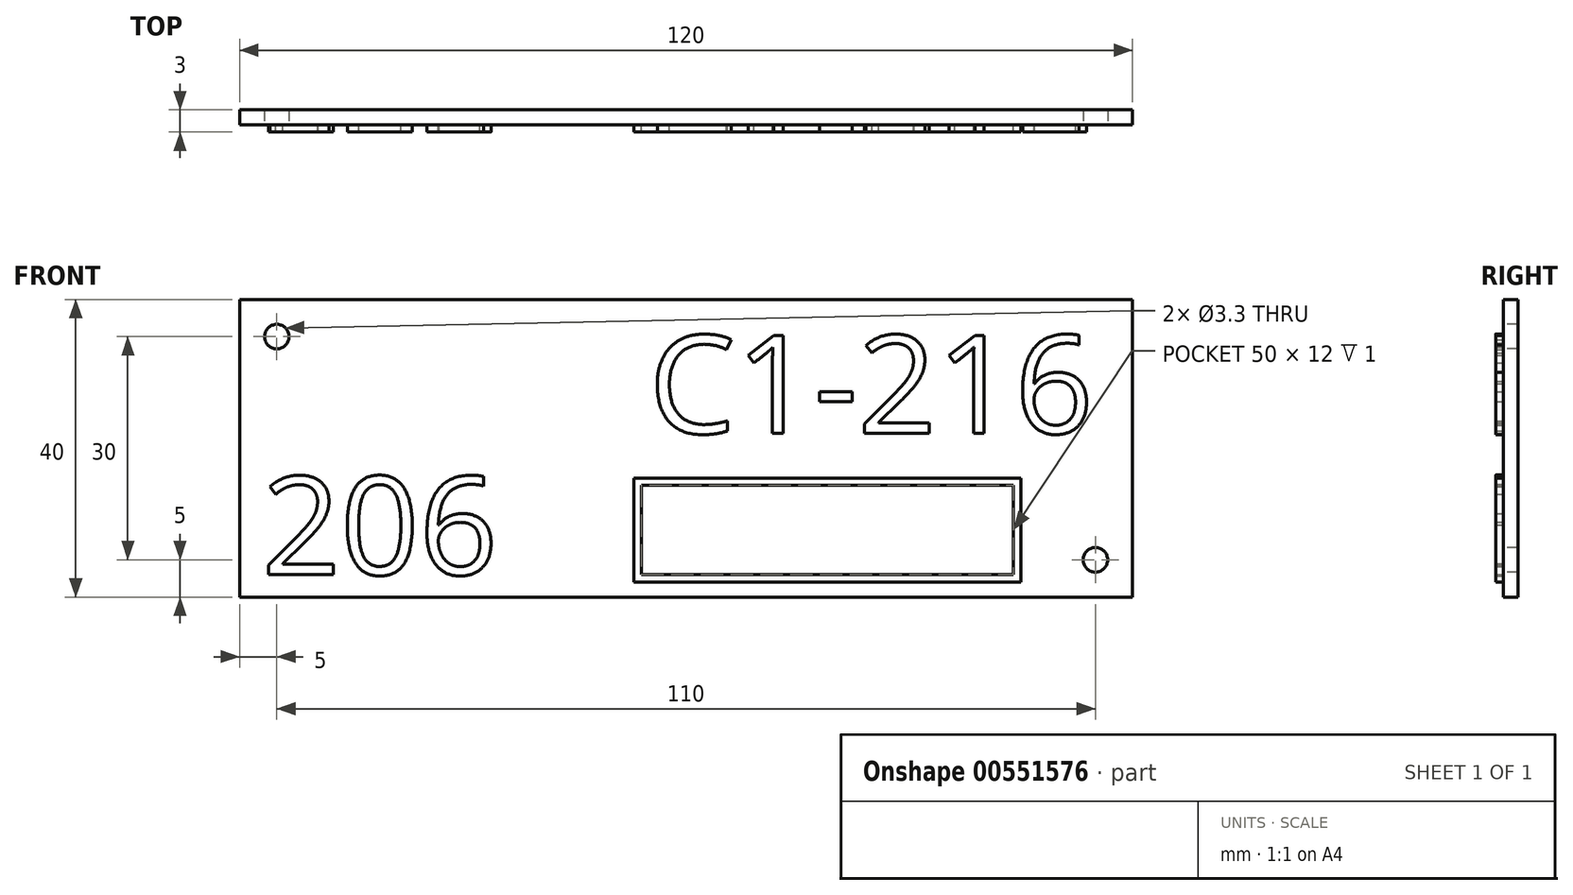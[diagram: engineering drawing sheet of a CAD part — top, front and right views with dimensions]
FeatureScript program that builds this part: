
annotation { "Feature Type Name" : "Feature", "Feature Type Description" : "" }
export const myFeature = defineFeature(function(context is Context, id is Id, definition is map)
    precondition{}
    {
        {
            var Q0;
            Q0=qCreatedBy(makeId("Front.planeOp"),FACE);
            var sketch = newSketch(context, id + "F0", { "sketchPlane" : qUnion([Q0])});
            skLineSegment(sketch, "E0.bottom", {"start": v(60, -20) * mm, "end": v(-60, -20) * mm});
            skLineSegment(sketch, "E0.top", {"start": v(60, 20) * mm, "end": v(-60, 20) * mm});
            skLineSegment(sketch, "E0.left", {"start": v(60, -20) * mm, "end": v(60, 20) * mm});
            skLineSegment(sketch, "E0.right", {"start": v(-60, -20) * mm, "end": v(-60, 20) * mm});
            skPoint(sketch, "E0.middle", {"position": v(0, 0) * mm});
            skSolve(sketch);
        }
        {
            var Q0;
            Q0=makeQuery(id+"F0.imprint","IMPRINT",FACE,{"disambiguationData":[TD([[makeQuery(id+"F0.imprint","IMPRINT",EDGE,{"derivedFrom":sQuery(id+"F0.wireOp",EDGE,"E0.bottom")}),-1.0]])]});
            extrude(context, id + "F1", {"entities" : qUnion([Q0]), "depth" : 2 * mm});
        }
        {
            var Q0;
            Q0=makeQuery(id+"F1.opExtrude","CAP_FACE",FACE,{"disambiguationData":[OSD([sQuery(id+"F0.wireOp",EDGE,"E0.bottom"),sQuery(id+"F0.wireOp",EDGE,"E0.top"),sQuery(id+"F0.wireOp",EDGE,"E0.left"),sQuery(id+"F0.wireOp",EDGE,"E0.right")])],"isStart":false});
            var sketch = newSketch(context, id + "F2", { "sketchPlane" : qUnion([Q0])});
            skPoint(sketch, "E1", {"position": v(-55, 15) * mm});
            skPoint(sketch, "E2", {"position": v(55, -15) * mm});
            skSolve(sketch);
        }
        {
            var Q0;
            Q0=sQuery(id+"F2.wireOp",VERTEX,"E1");
            var Q1;
            Q1=sQuery(id+"F2.wireOp",VERTEX,"E2");
            var Q2;
            Q2=makeQuery(id+"F1.opExtrude","SWEPT_BODY",BODY,{"disambiguationData":[OSD([sQuery(id+"F0.wireOp",EDGE,"E0.bottom"),sQuery(id+"F0.wireOp",EDGE,"E0.top"),sQuery(id+"F0.wireOp",EDGE,"E0.left"),sQuery(id+"F0.wireOp",EDGE,"E0.right")])]});
            hole(context, id + "F3", {"style" : HoleStyle.SIMPLE, "endStyle" : HoleEndStyle.THROUGH, "holeDiameter" : 3.3 * mm, "locations" : qUnion([Q0, Q1]), "scope" : qUnion([Q2]), "isTappedThrough" : true});
        }
        {
            var Q0;
            Q0=makeQuery(id+"F1.opExtrude","CAP_FACE",FACE,{"disambiguationData":[OSD([sQuery(id+"F0.wireOp",EDGE,"E0.bottom"),sQuery(id+"F0.wireOp",EDGE,"E0.top"),sQuery(id+"F0.wireOp",EDGE,"E0.left"),sQuery(id+"F0.wireOp",EDGE,"E0.right")])],"isStart":false});
            var sketch = newSketch(context, id + "F4", { "sketchPlane" : qUnion([Q0])});
            skText(sketch, "E3", { "text": "C1-216", "fontName": "OpenSans-Regular.ttf"});
            const initialGuessF4  = {"E3": [-0.005, 0.002, 1, 0, 0.01327]};
            skSetInitialGuess(sketch, initialGuessF4);
            skSolve(sketch);
        }
        {
            var Q0;
            Q0=qSketchRegion(id+"F4",true);
            extrude(context, id + "F5", {"entities" : qUnion([Q0]), "operationType" : NewBodyOperationType.ADD, "depth" : 1 * mm});
        }
        {
            var Q0;
            {var subQ0=sQuery(id+"F0.wireOp",EDGE,"E0.top");var subQ1=sQuery(id+"F0.wireOp",EDGE,"E0.left");var subQ2=sQuery(id+"F0.wireOp",EDGE,"E0.right");var subQ3=sQuery(id+"F0.wireOp",EDGE,"E0.bottom");Q0=makeQuery(id+"F5.boolean.opBoolean","SPLIT",FACE,{"disambiguationData":[TD([makeQuery(id+"F1.opExtrude","SWEPT_FACE",FACE,{"disambiguationData":[OSD([subQ3])]})])],"derivedFrom":makeQuery(id+"F1.opExtrude","CAP_FACE",FACE,{"disambiguationData":[OSD([subQ3,subQ0,subQ1,subQ2])],"isStart":false})});}
            var sketch = newSketch(context, id + "F6", { "sketchPlane" : qUnion([Q0])});
            skText(sketch, "E4", { "text": "206", "fontName": "OpenSans-Regular.ttf"});
            const initialGuessF6  = {"E4": [-0.057, -0.017, 1, 0, 0.0133]};
            skSetInitialGuess(sketch, initialGuessF6);
            skSolve(sketch);
        }
        {
            var Q0;
            Q0=qSketchRegion(id+"F6",true);
            extrude(context, id + "F7", {"entities" : qUnion([Q0]), "operationType" : NewBodyOperationType.ADD, "depth" : 1 * mm});
        }
        {
            var Q0;
            {var subQ46=sQuery(id+"F0.wireOp",EDGE,"E0.top");var subQ48=sQuery(id+"F0.wireOp",EDGE,"E0.left");var subQ66=sQuery(id+"F0.wireOp",EDGE,"E0.right");var subQ76=sQuery(id+"F0.wireOp",EDGE,"E0.bottom");var subQ77=makeQuery(id+"F1.opExtrude","SWEPT_FACE",FACE,{"disambiguationData":[OSD([subQ76])]});Q0=makeQuery(id+"F7.boolean.opBoolean","SPLIT",FACE,{"disambiguationData":[TD([subQ77])],"derivedFrom":makeQuery(id+"F5.boolean.opBoolean","SPLIT",FACE,{"disambiguationData":[TD([subQ77])],"derivedFrom":makeQuery(id+"F1.opExtrude","CAP_FACE",FACE,{"disambiguationData":[OSD([subQ76,subQ46,subQ48,subQ66])],"isStart":false})})});}
            var sketch = newSketch(context, id + "F8", { "sketchPlane" : qUnion([Q0])});
            skLineSegment(sketch, "E5.bottom", {"start": v(45, -18) * mm, "end": v(-7, -18) * mm});
            skLineSegment(sketch, "E5.top", {"start": v(45, -4) * mm, "end": v(-7, -4) * mm});
            skLineSegment(sketch, "E5.left", {"start": v(45, -18) * mm, "end": v(45, -4) * mm});
            skLineSegment(sketch, "E5.right", {"start": v(-7, -18) * mm, "end": v(-7, -4) * mm});
            skPoint(sketch, "E5.middle", {"position": v(19, -11) * mm});
            skLineSegment(sketch, "E6.0", {"start": v(44, -5) * mm, "end": v(-6, -5) * mm});
            skLineSegment(sketch, "E6.1", {"start": v(44, -17) * mm, "end": v(44, -5) * mm});
            skLineSegment(sketch, "E6.2", {"start": v(44, -17) * mm, "end": v(-6, -17) * mm});
            skLineSegment(sketch, "E6.3", {"start": v(-6, -17) * mm, "end": v(-6, -5) * mm});
            skSolve(sketch);
        }
        {
            var Q0;
            Q0=makeQuery(id+"F8.imprint","IMPRINT",FACE,{"disambiguationData":[TD([[makeQuery(id+"F8.imprint","IMPRINT",EDGE,{"derivedFrom":sQuery(id+"F8.wireOp",EDGE,"E5.bottom")}),-1.0]])]});
            extrude(context, id + "F9", {"entities" : qUnion([Q0]), "operationType" : NewBodyOperationType.ADD, "depth" : 1 * mm});
        }
    });
